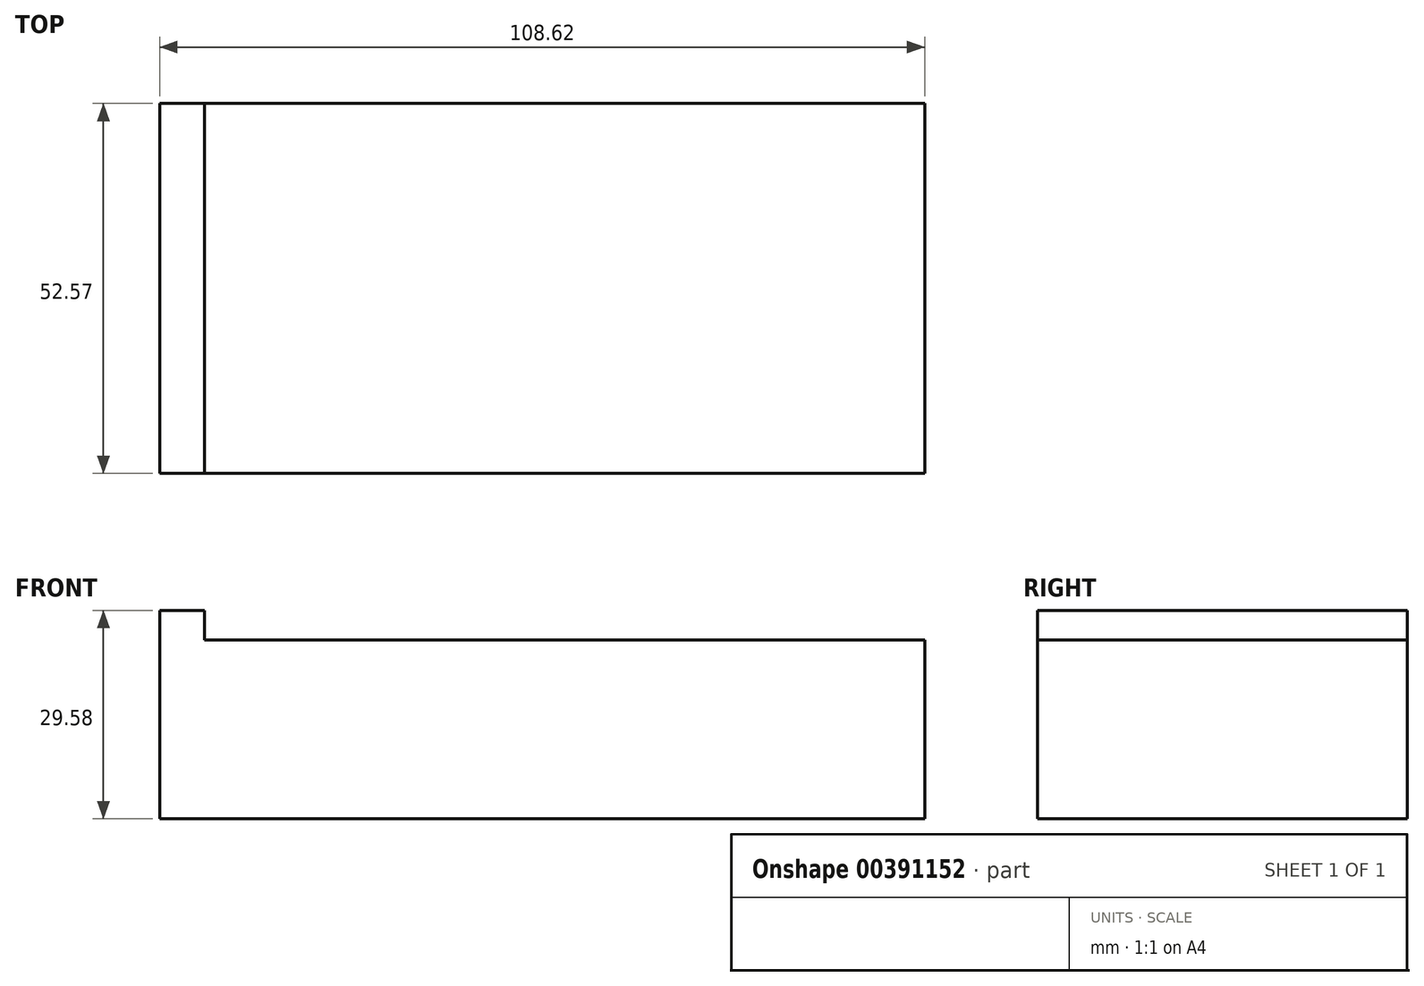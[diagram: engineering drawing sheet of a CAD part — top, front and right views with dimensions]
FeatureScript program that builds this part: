
annotation { "Feature Type Name" : "Feature", "Feature Type Description" : "" }
export const myFeature = defineFeature(function(context is Context, id is Id, definition is map)
    precondition{}
    {
        {
            var Q0;
            Q0=qCreatedBy(makeId("Top.planeOp"),FACE);
            var sketch = newSketch(context, id + "F0", { "sketchPlane" : qUnion([Q0])});
            skLineSegment(sketch, "E0.bottom", {"start": v(0, 0) * mm, "end": v(-102.27, 0) * mm});
            skLineSegment(sketch, "E0.top", {"start": v(0, -52.57) * mm, "end": v(-102.27, -52.57) * mm});
            skLineSegment(sketch, "E0.left", {"start": v(0, 0) * mm, "end": v(0, -52.57) * mm});
            skLineSegment(sketch, "E0.right", {"start": v(-102.27, 0) * mm, "end": v(-102.27, -52.57) * mm});
            skSolve(sketch);
        }
        {
            var Q0;
            Q0=makeQuery(id+"F0.imprint","IMPRINT",FACE,{"disambiguationData":[TD([[makeQuery(id+"F0.imprint","IMPRINT",EDGE,{"derivedFrom":sQuery(id+"F0.wireOp",EDGE,"E0.bottom")}),1.0]])]});
            extrude(context, id + "F1", {"entities" : qUnion([Q0]), "depth" : 25.4 * mm});
        }
        {
            var Q0;
            Q0=makeQuery(id+"F1.opExtrude","SWEPT_FACE",FACE,{"disambiguationData":[OSD([sQuery(id+"F0.wireOp",EDGE,"E0.right")])]});
            var sketch = newSketch(context, id + "F2", { "sketchPlane" : qUnion([Q0])});
            skLineSegment(sketch, "E1", {"start": v(0, 0) * mm, "end": v(0, 29.58) * mm});
            skLineSegment(sketch, "E2", {"start": v(0, 29.58) * mm, "end": v(52.57, 29.58) * mm});
            skLineSegment(sketch, "E3", {"start": v(52.57, 29.58) * mm, "end": v(52.57, 0) * mm});
            skLineSegment(sketch, "E4", {"start": v(52.57, 0) * mm, "end": v(18.65, 0) * mm});
            skLineSegment(sketch, "E5", {"start": v(18.65, 0) * mm, "end": v(0, 0) * mm});
            skSolve(sketch);
        }
        {
            var Q0;
            Q0 = qSketchRegion(id + "F2", true);
            extrude(context, id + "F3", {"entities" : qUnion([Q0]), "operationType" : NewBodyOperationType.ADD, "depth" : 6.35 * mm});
        }
    });
